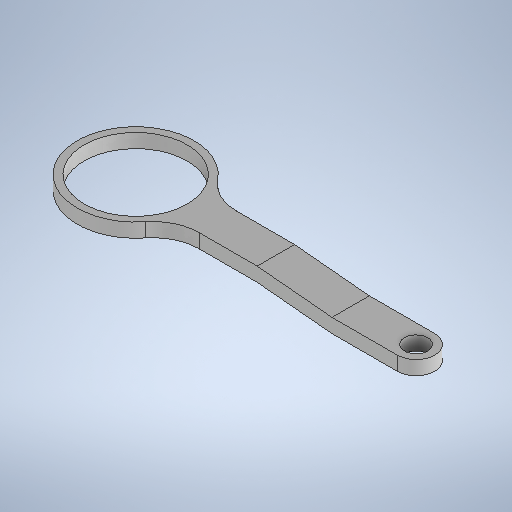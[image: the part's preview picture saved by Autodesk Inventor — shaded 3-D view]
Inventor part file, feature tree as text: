
AUTODESK INVENTOR PART (.ipt)
format: ipt  version: 2025.1 (Build 291241000, 241)  size: 297,984 bytes
history: native  units: mm
features: sketch x4, extrude x3, plane x1, hole x1
ambient origin geometry x8: Origin, YZ Plane, XZ Plane, XY Plane, X Axis, Y Axis, Z Axis, Center Point
bodies: Solid1 (feature_tree)
feature tree (9):
  sketch  "Sketch1"  dims[d0=25.0mm d1=22.0mm]
  extrude  "Extrusion1"  Depth=22.0mm
  plane  "Work Plane3"
  extrude  "Extrusion3"  Depth=10.0mm
  extrude  "Extrusion4"  Depth=3.0mm TaperAngle=0.0deg
  hole  "Hole1"  [1 undecoded]
  sketch  "Sketch7"  dims[d2=4.0mm d3=10.0mm]
  sketch  "Sketch8"  dims[d4=60.0mm d5=3.0mm d6=0.0mm]
  sketch  "Sketch9"  dims[d17=42.5mm d18=0.0mm d19=1.5mm d20=14.0mm d21=60.0mm d22=3.0mm d23=8.0mm d24=0.0mm d25=4.0mm d26=8.0mm d27=0.0mm d28=5.0mm d29=6.0mm d30=4.0mm d31=2.0mm d32=90.0deg d33=8.0mm d34=0.0mm]
note: 1 required parameter value undecoded (feature->parameter linkage not recoverable at this tier; creation-order binding heuristic only, values carry confidence <= 0.55)
